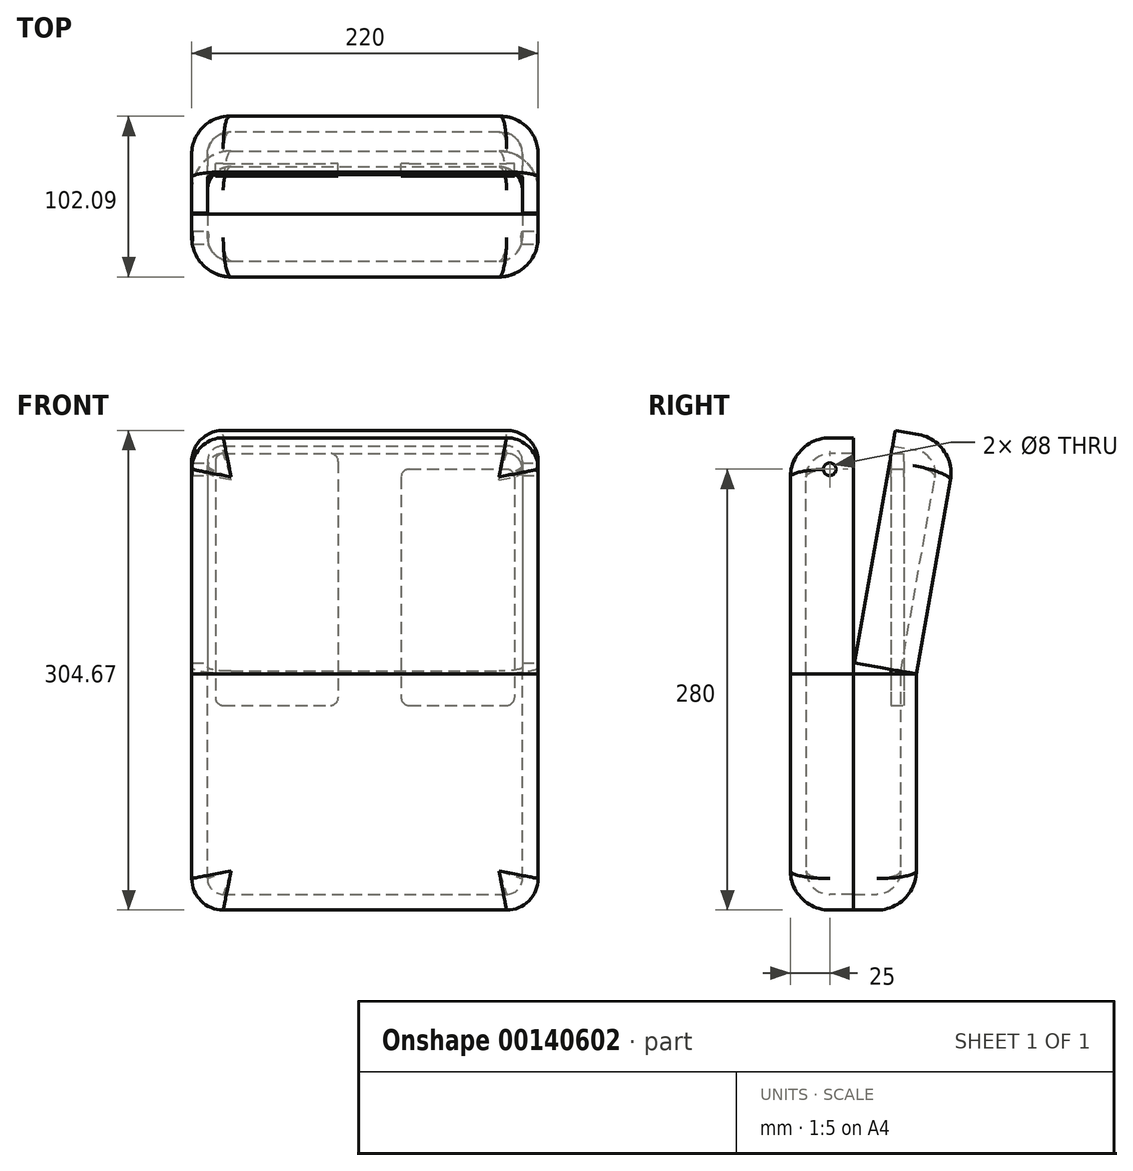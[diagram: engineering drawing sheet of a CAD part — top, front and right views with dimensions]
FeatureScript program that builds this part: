
annotation { "Feature Type Name" : "Feature", "Feature Type Description" : "" }
export const myFeature = defineFeature(function(context is Context, id is Id, definition is map)
    precondition{}
    {
        {
            var Q0;
            Q0=qCreatedBy(makeId("Front.planeOp"),FACE);
            var sketch = newSketch(context, id + "F0", { "sketchPlane" : qUnion([Q0])});
            skLineSegment(sketch, "E0.bottom", {"start": v(-90, 140) * mm, "end": v(-22, 140) * mm});
            skLineSegment(sketch, "E0.top", {"start": v(-90, -20) * mm, "end": v(-22, -20) * mm});
            skLineSegment(sketch, "E0.left", {"start": v(-95, 135) * mm, "end": v(-95, -15) * mm});
            skLineSegment(sketch, "E0.right", {"start": v(-17, 135) * mm, "end": v(-17, -15) * mm});
            skPoint(sketch, "E1.visualSharp", {"position": v(-95, 140) * mm});
            skArc(sketch, "E1.filletArc", {"start": v(-90, 140) * mm, "mid": v(-93.54, 138.54) * mm, "end": v(-95, 135) * mm});
            skPoint(sketch, "E2.visualSharp", {"position": v(-17, 140) * mm});
            skArc(sketch, "E2.filletArc", {"start": v(-17, 135) * mm, "mid": v(-18.46, 138.54) * mm, "end": v(-22, 140) * mm});
            skPoint(sketch, "E3.visualSharp", {"position": v(-17, -20) * mm});
            skArc(sketch, "E3.filletArc", {"start": v(-22, -20) * mm, "mid": v(-18.46, -18.54) * mm, "end": v(-17, -15) * mm});
            skPoint(sketch, "E4.visualSharp", {"position": v(-95, -20) * mm});
            skArc(sketch, "E4.filletArc", {"start": v(-95, -15) * mm, "mid": v(-93.54, -18.54) * mm, "end": v(-90, -20) * mm});
            skLineSegment(sketch, "E5.bottom", {"start": v(28, 130) * mm, "end": v(90, 130) * mm});
            skLineSegment(sketch, "E5.top", {"start": v(28, -20) * mm, "end": v(90, -20) * mm});
            skLineSegment(sketch, "E5.left", {"start": v(23, 125) * mm, "end": v(23, -15) * mm});
            skLineSegment(sketch, "E5.right", {"start": v(95, 125) * mm, "end": v(95, -15) * mm});
            skPoint(sketch, "E6.visualSharp", {"position": v(23, 130) * mm});
            skArc(sketch, "E6.filletArc", {"start": v(28, 130) * mm, "mid": v(24.46, 128.54) * mm, "end": v(23, 125) * mm});
            skPoint(sketch, "E7.visualSharp", {"position": v(95, 130) * mm});
            skArc(sketch, "E7.filletArc", {"start": v(95, 125) * mm, "mid": v(93.54, 128.54) * mm, "end": v(90, 130) * mm});
            skPoint(sketch, "E8.visualSharp", {"position": v(95, -20) * mm});
            skArc(sketch, "E8.filletArc", {"start": v(90, -20) * mm, "mid": v(93.54, -18.54) * mm, "end": v(95, -15) * mm});
            skPoint(sketch, "E9.visualSharp", {"position": v(23, -20) * mm});
            skArc(sketch, "E9.filletArc", {"start": v(23, -15) * mm, "mid": v(24.46, -18.54) * mm, "end": v(28, -20) * mm});
            skSolve(sketch);
        }
        {
            var Q0;
            Q0 = qSketchRegion(id + "F0", true);
            extrude(context, id + "F1", {"entities" : qUnion([Q0]), "depth" : 16 * mm, "hasSecondDirection" : true, "secondDirectionOppositeDirection" : false, "secondDirectionDepth" : 8 * mm});
        }
        {
            var Q0;
            Q0=qCreatedBy(makeId("Front.planeOp"),FACE);
            var sketch = newSketch(context, id + "F2", { "sketchPlane" : qUnion([Q0])});
            skLineSegment(sketch, "E10.bottom", {"start": v(-90, 150) * mm, "end": v(90, 150) * mm});
            skLineSegment(sketch, "E10.top", {"start": v(-110, 0) * mm, "end": v(110, 0) * mm});
            skLineSegment(sketch, "E10.left", {"start": v(-110, 130) * mm, "end": v(-110, 0) * mm});
            skLineSegment(sketch, "E10.right", {"start": v(110, 130) * mm, "end": v(110, 0) * mm});
            skPoint(sketch, "E11.visualSharp", {"position": v(-110, 150) * mm});
            skArc(sketch, "E11.filletArc", {"start": v(-90, 150) * mm, "mid": v(-104.14, 144.14) * mm, "end": v(-110, 130) * mm});
            skPoint(sketch, "E12.visualSharp", {"position": v(110, 150) * mm});
            skArc(sketch, "E12.filletArc", {"start": v(110, 130) * mm, "mid": v(104.14, 144.14) * mm, "end": v(90, 150) * mm});
            skSolve(sketch);
        }
        {
            var Q0;
            Q0 = qSketchRegion(id + "F2", true);
            extrude(context, id + "F7", {"entities" : qUnion([Q0]), "depth" : 40 * mm});
        }
        {
            var Q0;
            Q0=makeQuery(id+"F7.opExtrude","CAP_EDGE",EDGE,{"disambiguationData":[OSD([sQuery(id+"F2.wireOp",EDGE,"E10.left")])],"isStart":true});
            fillet(context, id + "F3", {"entities" : qUnion([Q0]), "radius" : 25 * mm, "tangentPropagation" : true, "allowEdgeOverflow" : false});
        }
        {
            var Q0;
            Q0=makeQuery(id+"F7.opExtrude","CAP_FACE",FACE,{"disambiguationData":[OSD([sQuery(id+"F2.wireOp",EDGE,"E10.bottom"),sQuery(id+"F2.wireOp",EDGE,"E10.top"),sQuery(id+"F2.wireOp",EDGE,"E10.left"),sQuery(id+"F2.wireOp",EDGE,"E10.right"),sQuery(id+"F2.wireOp",EDGE,"E11.filletArc"),sQuery(id+"F2.wireOp",EDGE,"E12.filletArc")])],"isStart":false});
            var Q1;
            Q1=makeQuery(id+"F7.opExtrude","SWEPT_FACE",FACE,{"disambiguationData":[OSD([sQuery(id+"F2.wireOp",EDGE,"E10.top")])]});
            shell(context, id + "F8", {"entities" : qUnion([Q0, Q1]), "thickness" : 10 * mm});
        }
        {
            var Q0;
            Q0=makeQuery(id+"F7.opExtrude","SWEPT_BODY",BODY,{"disambiguationData":[OSD([sQuery(id+"F2.wireOp",EDGE,"E10.bottom"),sQuery(id+"F2.wireOp",EDGE,"E10.top"),sQuery(id+"F2.wireOp",EDGE,"E10.left"),sQuery(id+"F2.wireOp",EDGE,"E10.right"),sQuery(id+"F2.wireOp",EDGE,"E11.filletArc"),sQuery(id+"F2.wireOp",EDGE,"E12.filletArc")])]});
            var Q1;
            Q1=qCreatedBy(makeId("Top.planeOp"),FACE);
            mirror(context, id + "F9", {"entities" : qUnion([Q0]), "mirrorPlane" : qUnion([Q1])});
        }
        {
            var Q0;
            Q0=makeQuery(id+"F9.opPattern","COPY",BODY,{"derivedFrom":makeQuery(id+"F7.opExtrude","SWEPT_BODY",BODY,{"disambiguationData":[OSD([sQuery(id+"F2.wireOp",EDGE,"E10.bottom"),sQuery(id+"F2.wireOp",EDGE,"E10.top"),sQuery(id+"F2.wireOp",EDGE,"E10.left"),sQuery(id+"F2.wireOp",EDGE,"E10.right"),sQuery(id+"F2.wireOp",EDGE,"E11.filletArc"),sQuery(id+"F2.wireOp",EDGE,"E12.filletArc")])]}),"instanceName":"1"});
            var Q1;
            Q1=makeQuery(id+"F7.opExtrude","SWEPT_BODY",BODY,{"disambiguationData":[OSD([sQuery(id+"F2.wireOp",EDGE,"E10.bottom"),sQuery(id+"F2.wireOp",EDGE,"E10.top"),sQuery(id+"F2.wireOp",EDGE,"E10.left"),sQuery(id+"F2.wireOp",EDGE,"E10.right"),sQuery(id+"F2.wireOp",EDGE,"E11.filletArc"),sQuery(id+"F2.wireOp",EDGE,"E12.filletArc")])]});
            var Q2;
            Q2=makeQuery(id+"F9.opPattern","COPY",FACE,{"derivedFrom":makeQuery(id+"F7.opExtrude","CAP_FACE",FACE,{"disambiguationData":[OSD([sQuery(id+"F2.wireOp",EDGE,"E10.bottom"),sQuery(id+"F2.wireOp",EDGE,"E10.top"),sQuery(id+"F2.wireOp",EDGE,"E10.left"),sQuery(id+"F2.wireOp",EDGE,"E10.right"),sQuery(id+"F2.wireOp",EDGE,"E11.filletArc"),sQuery(id+"F2.wireOp",EDGE,"E12.filletArc")])],"isStart":false}),"instanceName":"1"});
            mirror(context, id + "F4", {"entities" : qUnion([Q0, Q1]), "mirrorPlane" : qUnion([Q2])});
        }
        {
            var Q0;
            Q0=makeQuery(id+"F7.opExtrude","SWEPT_BODY",BODY,{"disambiguationData":[OSD([sQuery(id+"F2.wireOp",EDGE,"E10.bottom"),sQuery(id+"F2.wireOp",EDGE,"E10.top"),sQuery(id+"F2.wireOp",EDGE,"E10.left"),sQuery(id+"F2.wireOp",EDGE,"E10.right"),sQuery(id+"F2.wireOp",EDGE,"E11.filletArc"),sQuery(id+"F2.wireOp",EDGE,"E12.filletArc")])]});
            var Q1;
            Q1=makeQuery(id+"F7.opExtrude","CAP_EDGE",EDGE,{"disambiguationData":[OSD([sQuery(id+"F2.wireOp",EDGE,"E10.top")])],"isStart":true});
            transform(context, id + "F5", {"entities" : qUnion([Q0]), "transformType" : TransformType.ROTATION, "transformAxis" : qUnion([Q1]), "angle" : 10 * degree, "oppositeDirection" : true, "makeCopy" : false});
        }
        {
            var Q0;
            Q0=makeQuery(id+"F4.opPattern","COPY",FACE,{"derivedFrom":makeQuery(id+"F7.opExtrude","SWEPT_FACE",FACE,{"disambiguationData":[OSD([sQuery(id+"F2.wireOp",EDGE,"E10.right")])]}),"instanceName":"1"});
            var sketch = newSketch(context, id + "F6", { "sketchPlane" : qUnion([Q0])});
            skCircle(sketch, "E13", {"center": v(-55, 130) * mm, "radius": 4 * mm});
            skSolve(sketch);
        }
        {
            var Q0;
            Q0 = qSketchRegion(id + "F6", true);
            var Q1;
            Q1=makeQuery(id+"F4.opPattern","COPY",FACE,{"derivedFrom":makeQuery(id+"F7.opExtrude","SWEPT_FACE",FACE,{"disambiguationData":[OSD([sQuery(id+"F2.wireOp",EDGE,"E10.left")])]}),"instanceName":"1"});
            extrude(context, id + "F10", {"entities" : qUnion([Q0]), "operationType" : NewBodyOperationType.REMOVE, "endBound" : BoundingType.UP_TO_SURFACE, "oppositeDirection" : true, "endBoundEntityFace" : qUnion([Q1]), "depth" : 25 * mm});
        }
    });
